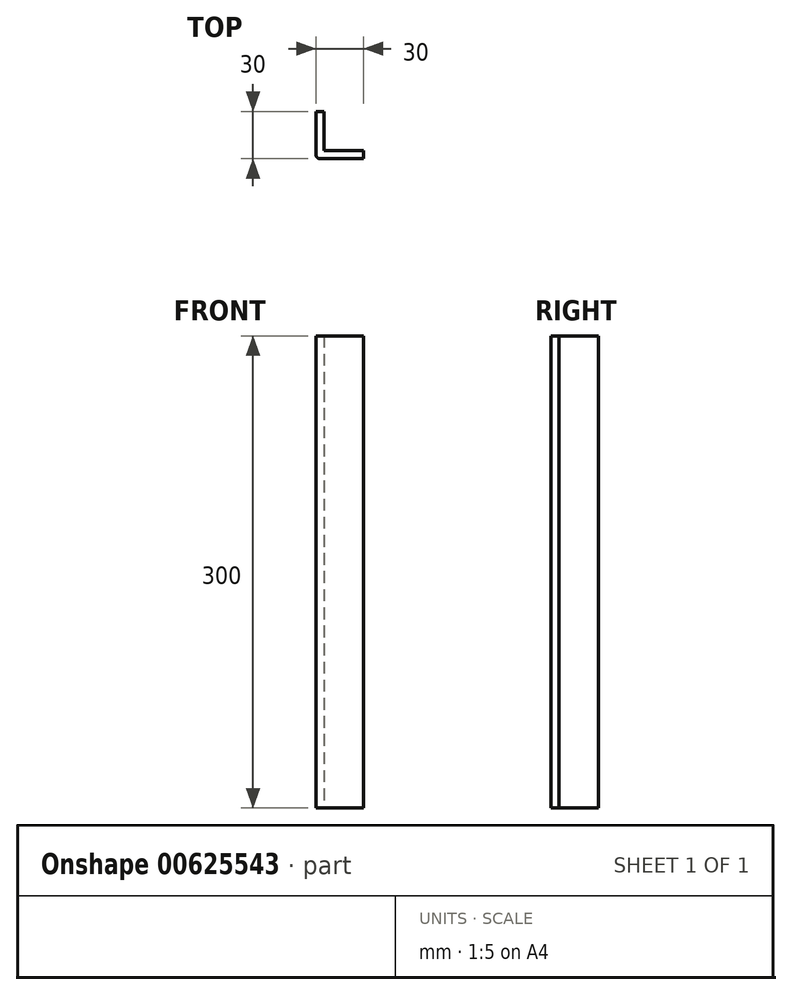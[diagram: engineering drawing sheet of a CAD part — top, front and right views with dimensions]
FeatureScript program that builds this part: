
annotation { "Feature Type Name" : "Feature", "Feature Type Description" : "" }
export const myFeature = defineFeature(function(context is Context, id is Id, definition is map)
    precondition{}
    {
        {
            var Q0;
            Q0=qCreatedBy(makeId("Top.planeOp"),FACE);
            var sketch = newSketch(context, id + "F0", { "sketchPlane" : qUnion([Q0])});
            skLineSegment(sketch, "E0.bottom", {"start": v(-15, 15) * mm, "end": v(-10, 15) * mm});
            skLineSegment(sketch, "E0.top", {"start": v(-12.5, -15) * mm, "end": v(15, -15) * mm});
            skLineSegment(sketch, "E0.left", {"start": v(-15, 15) * mm, "end": v(-15, -12.5) * mm});
            skLineSegment(sketch, "E0.right", {"start": v(15, -10) * mm, "end": v(15, -15) * mm});
            skPoint(sketch, "E0.middle", {"position": v(0, 0) * mm});
            skLineSegment(sketch, "E1", {"start": v(-10, 15) * mm, "end": v(-10, -10) * mm});
            skLineSegment(sketch, "E2", {"start": v(-10, -10) * mm, "end": v(15, -10) * mm});
            skPoint(sketch, "E3.visualSharp", {"position": v(-10, -10) * mm});
            skLineSegment(sketch, "E3.filletArc", {"start": v(-10, -10) * mm, "end": v(-10, -10) * mm});
            skPoint(sketch, "E4.visualSharp", {"position": v(-15, -15) * mm});
            skArc(sketch, "E4.filletArc", {"start": v(-15, -12.5) * mm, "mid": v(-14.27, -14.27) * mm, "end": v(-12.5, -15) * mm});
            skPoint(sketch, "E5.orphan", {"position": v(15, 15) * mm});
            skSolve(sketch);
        }
        {
            var Q0;
            Q0 = qSketchRegion(id + "F0", true);
            extrude(context, id + "F1", {"entities" : qUnion([Q0]), "depth" : 300 * mm, "offsetDistance" : 25 * mm});
        }
    });
